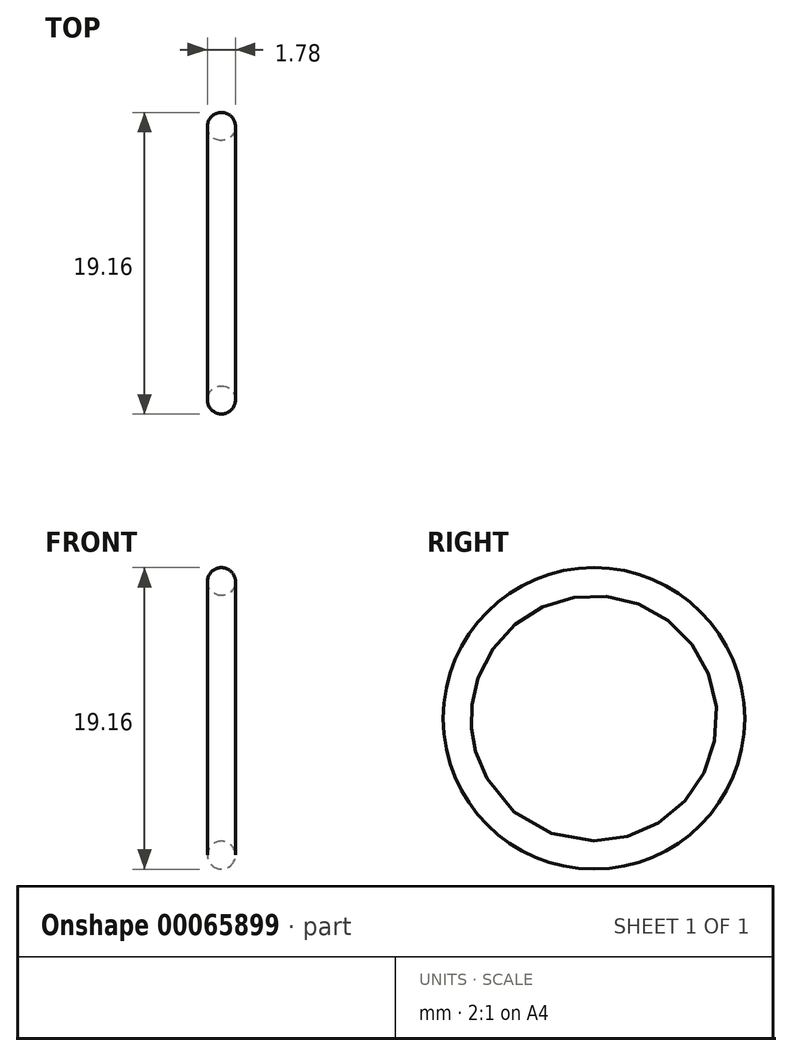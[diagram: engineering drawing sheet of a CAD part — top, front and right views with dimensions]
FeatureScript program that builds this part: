
annotation { "Feature Type Name" : "Feature", "Feature Type Description" : "" }
export const myFeature = defineFeature(function(context is Context, id is Id, definition is map)
    precondition{}
    {
        {
            var Q0;
            Q0=qCreatedBy(makeId("Front.planeOp"),FACE);
            var sketch = newSketch(context, id + "F0", { "sketchPlane" : qUnion([Q0])});
            skLineSegment(sketch, "E0", {"start": v(0, 0) * mm, "end": v(-6.06, 0) * mm, "construction": true});
            skCircle(sketch, "E1", {"center": v(0, 8.69) * mm, "radius": 0.89 * mm});
            skSolve(sketch);
        }
        {
            var Q0;
            Q0=makeQuery(id+"F0.imprint","IMPRINT",FACE,{"disambiguationData":[TD([[makeQuery(id+"F0.imprint","IMPRINT",EDGE,{"derivedFrom":sQuery(id+"F0.wireOp",EDGE,"E1")}),1.0]])]});
            var Q1;
            Q1=sQuery(id+"F0.wireOp",EDGE,"E0");
            revolve(context, id + "F1", {"entities" : qUnion([Q0]), "axis" : qUnion([Q1]), "revolveType" : RevolveType.FULL});
        }
    });
